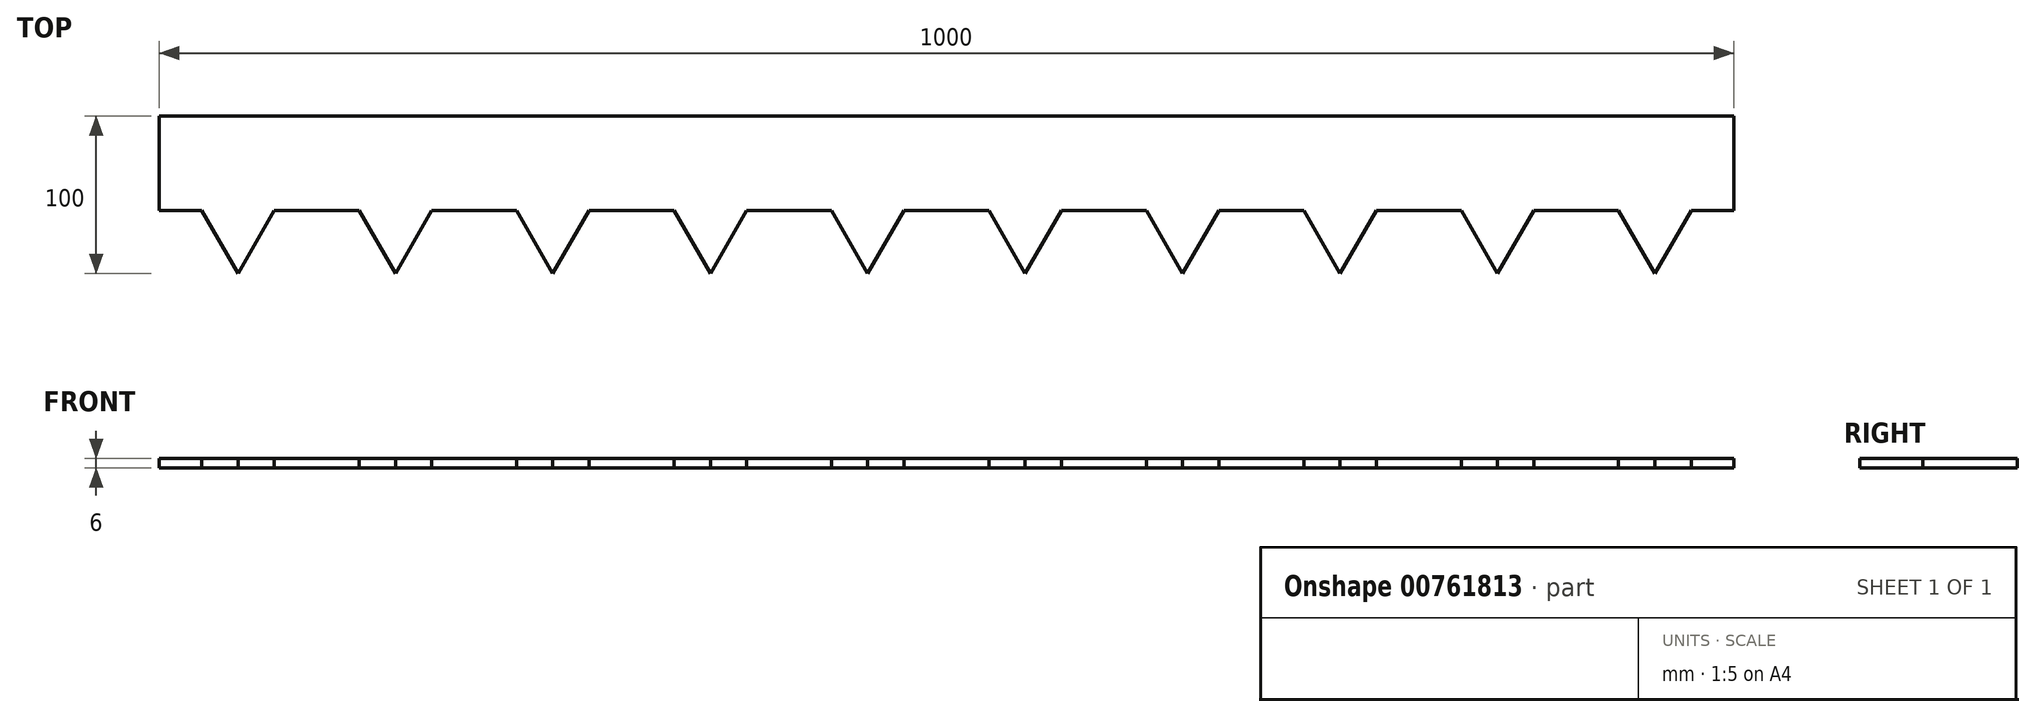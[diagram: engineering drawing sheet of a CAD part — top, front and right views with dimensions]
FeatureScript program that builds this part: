
annotation { "Feature Type Name" : "Feature", "Feature Type Description" : "" }
export const myFeature = defineFeature(function(context is Context, id is Id, definition is map)
    precondition{}
    {
        {
            var Q0;
            Q0=qCreatedBy(makeId("Top.planeOp"),FACE);
            var sketch = newSketch(context, id + "F0", { "sketchPlane" : qUnion([Q0])});
            skLineSegment(sketch, "E0", {"start": v(0, 0) * mm, "end": v(1000, 0) * mm});
            skLineSegment(sketch, "E1", {"start": v(1000, 0) * mm, "end": v(1000, -60) * mm});
            skLineSegment(sketch, "E2", {"start": v(1000, -60) * mm, "end": v(0, -60) * mm});
            skLineSegment(sketch, "E3", {"start": v(0, -60) * mm, "end": v(0, 0) * mm});
            skLineSegment(sketch, "E4", {"start": v(50, -29.94) * mm, "end": v(50, -100) * mm, "construction": true});
            skLineSegment(sketch, "E5", {"start": v(50, -100) * mm, "end": v(81.37, -45.67) * mm});
            skLineSegment(sketch, "E6.MirrorCS", {"start": v(50, -100) * mm, "end": v(18.63, -45.67) * mm});
            skLineSegment(sketch, "E7.1.0.0", {"start": v(150, -100) * mm, "end": v(118.63, -45.67) * mm});
            skLineSegment(sketch, "E7.1.0.1", {"start": v(150, -100) * mm, "end": v(181.37, -45.67) * mm});
            skLineSegment(sketch, "E7.2.0.0", {"start": v(250, -100) * mm, "end": v(218.63, -45.67) * mm});
            skLineSegment(sketch, "E7.2.0.1", {"start": v(250, -100) * mm, "end": v(281.37, -45.67) * mm});
            skLineSegment(sketch, "E7.3.0.0", {"start": v(350, -100) * mm, "end": v(318.63, -45.67) * mm});
            skLineSegment(sketch, "E7.3.0.1", {"start": v(350, -100) * mm, "end": v(381.37, -45.67) * mm});
            skLineSegment(sketch, "E7.4.0.0", {"start": v(450, -100) * mm, "end": v(418.63, -45.67) * mm});
            skLineSegment(sketch, "E7.4.0.1", {"start": v(450, -100) * mm, "end": v(481.37, -45.67) * mm});
            skLineSegment(sketch, "E7.5.0.0", {"start": v(550, -100) * mm, "end": v(518.63, -45.67) * mm});
            skLineSegment(sketch, "E7.5.0.1", {"start": v(550, -100) * mm, "end": v(581.37, -45.67) * mm});
            skLineSegment(sketch, "E7.6.0.0", {"start": v(650, -100) * mm, "end": v(618.63, -45.67) * mm});
            skLineSegment(sketch, "E7.6.0.1", {"start": v(650, -100) * mm, "end": v(681.37, -45.67) * mm});
            skLineSegment(sketch, "E7.7.0.0", {"start": v(750, -100) * mm, "end": v(718.63, -45.67) * mm});
            skLineSegment(sketch, "E7.7.0.1", {"start": v(750, -100) * mm, "end": v(781.37, -45.67) * mm});
            skLineSegment(sketch, "E7.8.0.0", {"start": v(850, -100) * mm, "end": v(818.63, -45.67) * mm});
            skLineSegment(sketch, "E7.8.0.1", {"start": v(850, -100) * mm, "end": v(881.37, -45.67) * mm});
            skLineSegment(sketch, "E7.9.0.0", {"start": v(950, -100) * mm, "end": v(918.63, -45.67) * mm});
            skLineSegment(sketch, "E7.9.0.1", {"start": v(950, -100) * mm, "end": v(981.37, -45.67) * mm});
            skLineSegment(sketch, "E7.direction1", {"start": v(50, -100) * mm, "end": v(150, -100) * mm, "construction": true});
            skSolve(sketch);
        }
        {
            var Q0;
            Q0 = qSketchRegion(id + "F0", true);
            extrude(context, id + "F1", {"entities" : qUnion([Q0]), "depth" : 6 * mm, "offsetDistance" : 25 * mm});
        }
    });
